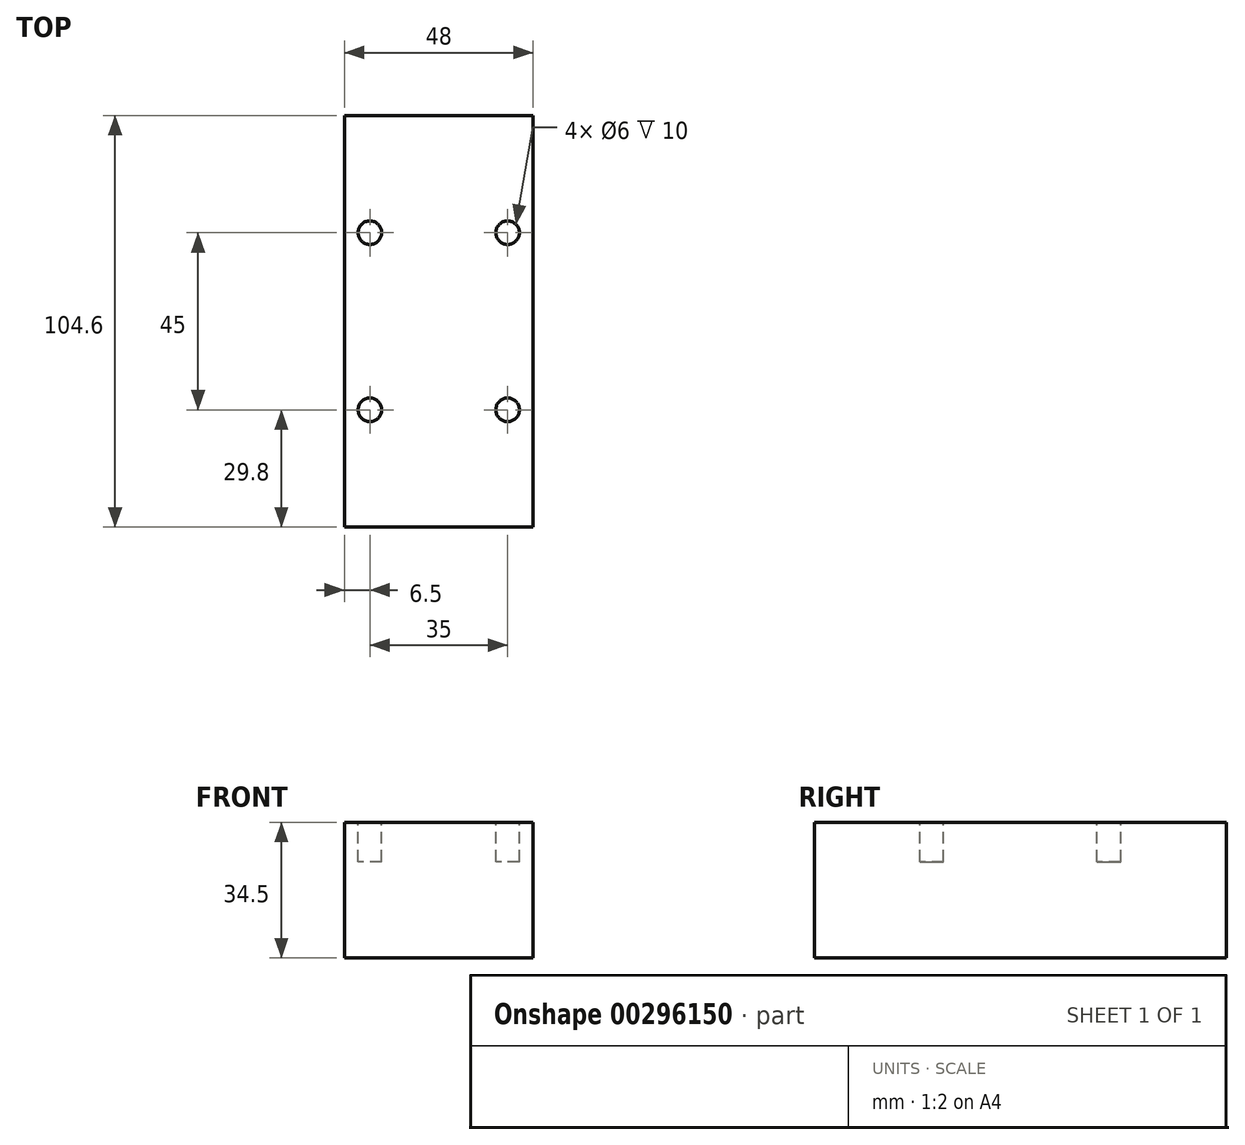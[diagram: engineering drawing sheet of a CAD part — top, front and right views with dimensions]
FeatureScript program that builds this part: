
annotation { "Feature Type Name" : "Feature", "Feature Type Description" : "" }
export const myFeature = defineFeature(function(context is Context, id is Id, definition is map)
    precondition{}
    {
        {
            var Q0;
            Q0=qCreatedBy(makeId("Front.planeOp"),FACE);
            var sketch = newSketch(context, id + "F0", { "sketchPlane" : qUnion([Q0])});
            skLineSegment(sketch, "E0.bottom", {"start": v(-24, 17.25) * mm, "end": v(24, 17.25) * mm});
            skLineSegment(sketch, "E0.top", {"start": v(-24, -17.25) * mm, "end": v(24, -17.25) * mm});
            skLineSegment(sketch, "E0.left", {"start": v(-24, 17.25) * mm, "end": v(-24, -17.25) * mm});
            skLineSegment(sketch, "E0.right", {"start": v(24, 17.25) * mm, "end": v(24, -17.25) * mm});
            skPoint(sketch, "E0.middle", {"position": v(0, 0) * mm});
            skSolve(sketch);
        }
        {
            var Q0;
            Q0=qSketchRegion(id+"F0",true);
            extrude(context, id + "F1", {"entities" : qUnion([Q0]), "oppositeDirection" : true, "depth" : 104.6 * mm});
        }
        {
            var Q0;
            Q0=makeQuery(id+"F1.opExtrude","SWEPT_FACE",FACE,{"disambiguationData":[OSD([sQuery(id+"F0.wireOp",EDGE,"E0.bottom")])]});
            var sketch = newSketch(context, id + "F2", { "sketchPlane" : qUnion([Q0])});
            skPoint(sketch, "E1.middle", {"position": v(0, 52.3) * mm});
            skLineSegment(sketch, "E2", {"start": v(0, 96.12) * mm, "end": v(-17.5, 96.12) * mm, "construction": true});
            skLineSegment(sketch, "E3", {"start": v(0, 96.12) * mm, "end": v(17.5, 96.12) * mm, "construction": true});
            skLineSegment(sketch, "E4", {"start": v(-17.5, 96.12) * mm, "end": v(-17.5, 13) * mm, "construction": true});
            skLineSegment(sketch, "E5", {"start": v(17.5, 96.12) * mm, "end": v(17.5, 13) * mm, "construction": true});
            skLineSegment(sketch, "E6", {"start": v(0, 52.3) * mm, "end": v(0, 74.8) * mm, "construction": true});
            skLineSegment(sketch, "E7", {"start": v(0, 52.3) * mm, "end": v(0, 29.8) * mm, "construction": true});
            skLineSegment(sketch, "E8", {"start": v(0, 74.8) * mm, "end": v(-17.5, 74.8) * mm, "construction": true});
            skCircle(sketch, "E9", {"center": v(-17.5, 74.8) * mm, "radius": 3 * mm});
            skCircle(sketch, "E10", {"center": v(-17.5, 29.8) * mm, "radius": 3 * mm});
            skCircle(sketch, "E11", {"center": v(17.5, 29.8) * mm, "radius": 3 * mm});
            skCircle(sketch, "E12", {"center": v(17.5, 74.8) * mm, "radius": 3 * mm});
            skPoint(sketch, "E12.centerSnap0", {"position": v(-8.75, 74.8) * mm});
            skSolve(sketch);
        }
        {
            var Q0;
            Q0=qSketchRegion(id+"F2",true);
            extrude(context, id + "F3", {"entities" : qUnion([Q0]), "operationType" : NewBodyOperationType.REMOVE, "oppositeDirection" : true, "depth" : 10 * mm});
        }
    });
